# Revit family: Wall connection piece 2R
name_source: partatom
category: Generic Models
revit_build: Autodesk Revit 2017 (Build: 20160225_1515(x64)
units: mm (PartAtom-declared; Revit-internal decimal feet)

## family parameters
Always vertical = No
Can host rebar = No
Cut with Voids When Loaded = No
Part Type = Normal
Room Calculation Point = No
Round Connector Dimension = Use Diameter
Shared = No
Work Plane-Based = Yes

## types (2) — shared parameters
Default Elevation = 1219 mm
Edition number = 1
Option 1 = Cable Tray Size : 60 x 60
Option 2 = Cable Tray Size : 60 x 100
Option 3 = Cable Tray Size : 60 x 150
Option 4 = Cable Tray Size : 100 x 150
Option 5 = Cable Tray Size : 100 x 250
Thickness = 2 mm  [stored 0.00656168 ft]

## per-type parameters (varying)
| type | RAL-9016 |
| RAL-9016 | Yes |
| Galvanized Steel | No |

note: column(s) folded — value = type name in every type: Product Material

type visibility flags (boolean, named after types; folded from table):
- RAL-9016: Yes: (none)
- Galvanized Steel: Yes: Galvanized Steel

note: [stored X ft] marks values corroborated as IEEE doubles in the binary element streams (Revit-internal decimal feet)

## geometry (parser evidence)
native form markers: Sweep x4
no freeform markers — native parametric forms only
